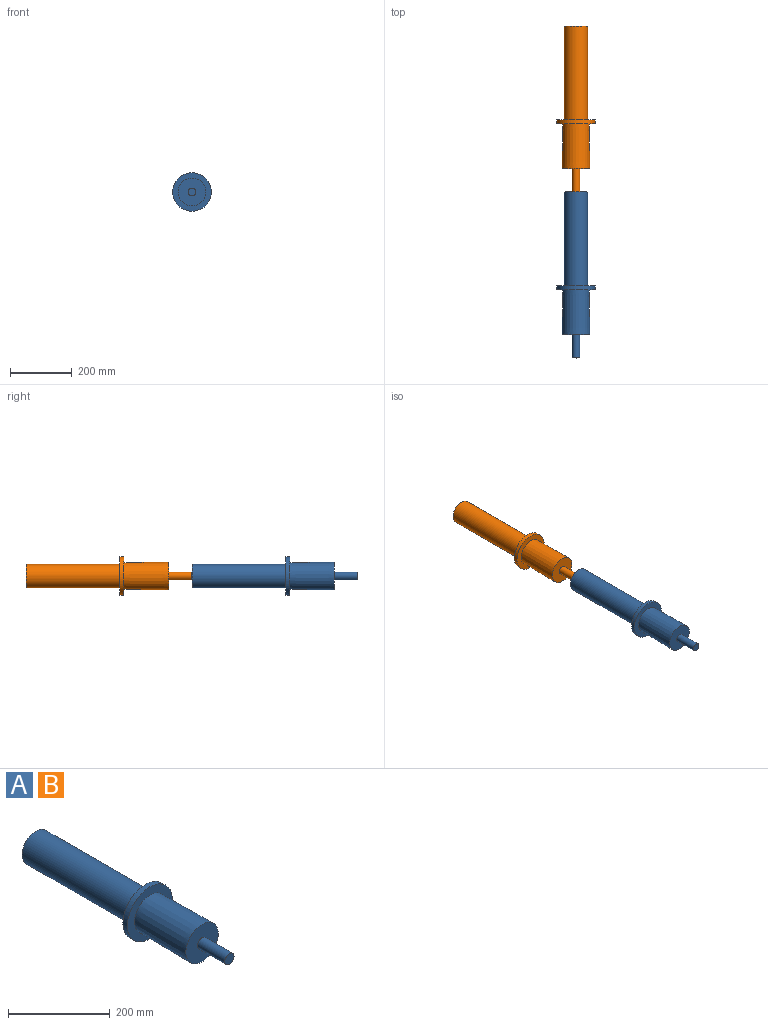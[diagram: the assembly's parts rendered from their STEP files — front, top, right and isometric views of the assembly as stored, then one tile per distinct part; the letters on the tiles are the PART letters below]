
ASSEMBLY  parts=2 mates=1
PART A: 9 faces, bbox 125x538.4x125 mm
  f0: plane 124.65x124.65mm, normal (0,1,0), area 7643.6mm2, adj f4,f5
  f1: plane 89.94x89.94mm, normal (0,-1,0), area 5845.9mm2, adj f2,f7
  f2: cone r=44.97mm half-angle=0.8deg, axis (0,-1,0), area 40000.4mm2, adj f1,f3
  f3: cone r=43.07mm half-angle=89.2deg, axis (0,1,0), area 6439.9mm2, adj f2,f4
  f4: cone r=62.49mm half-angle=0.8deg, axis (0,-1,0), area 4912.2mm2, adj f0,f3
  f5: cylinder r=38.1mm len=304.8mm, axis (0,-1,0), area 72965.9mm2, adj f0,f6
  f6: plane 76.2x76.2mm, normal (0,1,0), area 4560.4mm2, adj f5
  f7: cylinder r=12.7mm len=76.2mm, axis (0,1,0), area 6080.5mm2, adj f1,f8
  f8: plane 25.4x25.4mm, normal (0,-1,0), area 506.7mm2, adj f7
PART B: same geometry as A
PLACE A t=(0,-538.39,0)mm
PLACE B at identity fixed
MATE fastened B.f7 <-> A.f5  axis (0,-1,0) through (-41.23,-214.73,0)mm
